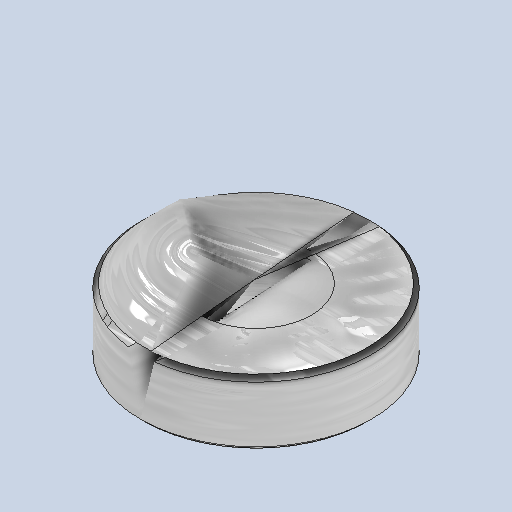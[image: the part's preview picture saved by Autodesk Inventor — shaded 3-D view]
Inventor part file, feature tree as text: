
AUTODESK INVENTOR PART (.ipt)
format: ipt  version: 2024 (Build 280153000, 153)  size: 169,984 bytes
history: native  units: in
note: dims shown in document units (in); Inventor stores cm internally (conversion verified against a paired STEP export)
features: chamfer x1
ambient origin geometry x8: Origin, YZ Plane, XZ Plane, XY Plane, X Axis, Y Axis, Z Axis, Center Point
bodies: Solid1 (feature_tree)
feature tree (1):
  chamfer  "Chamfer1"  [1 undecoded]
note: 1 required parameter value undecoded (feature->parameter linkage not recoverable at this tier; creation-order binding heuristic only, values carry confidence <= 0.55)
